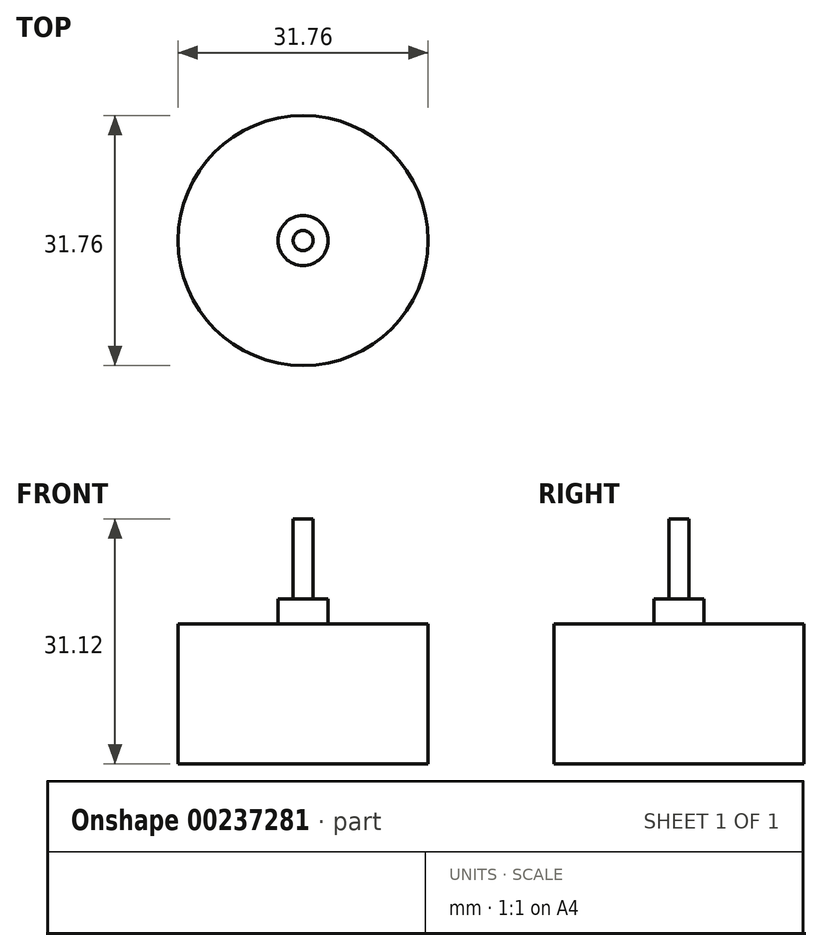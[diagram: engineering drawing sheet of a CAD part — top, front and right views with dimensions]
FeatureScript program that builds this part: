
annotation { "Feature Type Name" : "Feature", "Feature Type Description" : "" }
export const myFeature = defineFeature(function(context is Context, id is Id, definition is map)
    precondition{}
    {
        {
            var Q0;
            Q0=qCreatedBy(makeId("Top.planeOp"),FACE);
            var sketch = newSketch(context, id + "F0", { "sketchPlane" : qUnion([Q0])});
            skCircle(sketch, "E0", {"center": v(0, 0) * mm, "radius": 15.88 * mm});
            skSolve(sketch);
        }
        {
            var Q0;
            Q0=makeQuery(id+"F0.imprint","IMPRINT",FACE,{"disambiguationData":[TD([[makeQuery(id+"F0.imprint","IMPRINT",EDGE,{"derivedFrom":sQuery(id+"F0.wireOp",EDGE,"E0")}),1.0]])]});
            extrude(context, id + "F1", {"entities" : qUnion([Q0]), "depth" : 17.78 * mm});
        }
        {
            var Q0;
            Q0=makeQuery(id+"F1.opExtrude","CAP_FACE",FACE,{"disambiguationData":[OSD([sQuery(id+"F0.wireOp",EDGE,"E0")])],"isStart":false});
            var sketch = newSketch(context, id + "F2", { "sketchPlane" : qUnion([Q0])});
            skCircle(sketch, "E1", {"center": v(0, 0) * mm, "radius": 3.18 * mm});
            skSolve(sketch);
        }
        {
            var Q0;
            Q0=makeQuery(id+"F2.imprint","IMPRINT",FACE,{"disambiguationData":[TD([[makeQuery(id+"F2.imprint","IMPRINT",EDGE,{"derivedFrom":sQuery(id+"F2.wireOp",EDGE,"E1")}),1.0]])]});
            extrude(context, id + "F3", {"entities" : qUnion([Q0]), "operationType" : NewBodyOperationType.ADD, "depth" : 3.17 * mm});
        }
        {
            var Q0;
            Q0=makeQuery(id+"F3.opExtrude","CAP_FACE",FACE,{"disambiguationData":[OSD([sQuery(id+"F2.wireOp",EDGE,"E1")])],"isStart":false});
            var sketch = newSketch(context, id + "F4", { "sketchPlane" : qUnion([Q0])});
            skCircle(sketch, "E2", {"center": v(0, 0) * mm, "radius": 1.27 * mm});
            skSolve(sketch);
        }
        {
            var Q0;
            Q0=makeQuery(id+"F4.imprint","IMPRINT",FACE,{"disambiguationData":[TD([[makeQuery(id+"F4.imprint","IMPRINT",EDGE,{"derivedFrom":sQuery(id+"F4.wireOp",EDGE,"E2")}),1.0]])]});
            var Q1;
            Q1=sQuery(id+"F4.wireOp",EDGE,"E2");
            extrude(context, id + "F5", {"entities" : qUnion([Q0]), "operationType" : NewBodyOperationType.ADD, "surfaceEntities" : qUnion([Q1]), "depth" : 10.16 * mm});
        }
    });
